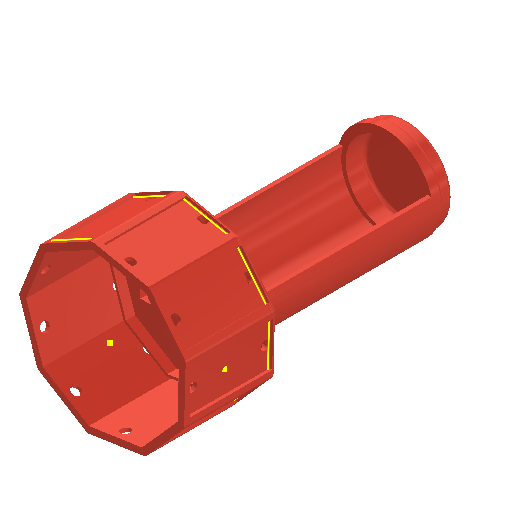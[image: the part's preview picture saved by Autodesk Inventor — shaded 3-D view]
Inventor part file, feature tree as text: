
AUTODESK INVENTOR PART (.ipt)
format: ipt  version: 2025 (Build 290162000, 162)  size: 719,872 bytes
history: native  units: in
note: dims shown in document units (in); Inventor stores cm internally (conversion verified against a paired STEP export)
features: sketch x28, extrude x24, fillet x7, direct_edit x2, pattern_circular x2, move_body x1, projected_geometry x1, other x1
ambient origin geometry x8: Origin, YZ Plane, XZ Plane, XY Plane, X Axis, Y Axis, Z Axis, Center Point
bodies: Solid1 (feature_tree), Body4 (feature_tree)
feature tree (66):
  direct_edit  "Direct Edit1"
  extrude  "Extrusion1"  Depth=0.2062in TaperAngle=0.0deg
  extrude  "Extrusion2"  Depth=0.1437in TaperAngle=0.0deg
  sketch  "Sketch3"  dims[d8=0.0787in d9=1.811in d10=0.0in]
  extrude  "Extrusion3"  Depth=0.0787in TaperAngle=0.0deg
  sketch  "Sketch6"  dims[d13=0.0591in d14=0.0in d15=0.1969in]
  extrude  "Extrusion4"  Depth=0.9449in
  extrude  "Extrusion5"  Depth=0.1969in
  pattern_circular  "Circular Pattern1"  Count=9  [1 undecoded]
  extrude  "Extrusion6"  Depth=0.0787in
  extrude  "Extrusion7"  Depth=0.0787in TaperAngle=0.0deg
  pattern_circular  "Circular Pattern2"  Count=9  [1 undecoded]
  fillet  "Fillet1"  Radius=0.1412in
  extrude  "Extrusion8"  Depth=0.063in
  extrude  "Extrusion9"  Depth=0.8312in TaperAngle=0.0deg
  extrude  "Extrusion10"  Depth=0.0787in
  extrude  "Extrusion11"  Depth=0.0787in TaperAngle=0.0deg
  direct_edit  "Direct Edit2"
  extrude  "Extrusion12"  Depth=1.1063in TaperAngle=0.0deg
  extrude  "Extrusion13"  Depth=0.4724in TaperAngle=0.0deg
  extrude  "Extrusion14"  Depth=0.0787in
  extrude  "Extrusion15"  Depth=1.2795in
  extrude  "Extrusion16"  Depth=0.0787in TaperAngle=0.0deg
  extrude  "Extrusion17"  Depth=0.0787in
  fillet  "Fillet2"  Radius=0.0787in
  fillet  "Fillet3"  Radius=0.0787in
  fillet  "Fillet4"  Radius=0.7338in
  fillet  "Fillet5"  Radius=0.3937in
  extrude  "Extrusion18"  Depth=0.0787in TaperAngle=0.0deg
  extrude  "Extrusion19"  Depth=0.1575in TaperAngle=0.0deg
  extrude  "Extrusion20"  Depth=0.1969in TaperAngle=0.0deg
  fillet  "Fillet6"  Radius=0.1781in
  sketch  "Sketch24"  dims[d78=1.3912in d79=0.1969in d80=0.0in d81=0.1781in d82=0.0in]
  extrude  "Extrusion22"  Depth=0.1575in
  fillet  "Fillet8"  Radius=1.9685in
  extrude  "Extrusion23"  Depth=1.9685in
  extrude  "Extrusion24"  [1 undecoded]
  extrude  "Extrusion25"  [1 undecoded]
  sketch  "Sketch30"
  sketch  "Sketch1"  dims[d0=0.0in d1=0.0in d2=-0.6875in d3=0.2062in d4=0.0in]
  sketch  "Sketch2"  dims[d5=1.1811in d6=0.1437in d7=0.0in]
  sketch  "Sketch5"  dims[d11=1.7323in d12=0.9449in]
  sketch  "Sketch7"  dims[d16=0.1969in]
  sketch  "Sketch8"  dims[d17=0.1841in d18=0.0in d19=3.5433in d20=2.4737in]
  sketch  "Sketch9"  dims[d22=0.0787in d23=0.315in]
  sketch  "Sketch10"  dims[d24=0.0787in d25=1.4409in d26=0.0in]
  sketch  "Sketch11"  dims[d27=1.9966in d28=0.0in d29=3.5433in d30=2.4737in d32=0.1412in]
  sketch  "Sketch12"  dims[d33=0.063in d34=0.063in]
  sketch  "Sketch13"  dims[d35=0.2756in d36=0.0in d37=0.8312in d38=0.0in]
  sketch  "Sketch14"  dims[d39=1.1063in d40=0.0in d41=0.0787in]
  sketch  "Sketch15"  dims[d42=0.0787in d43=0.1688in d44=0.0in]
  sketch  "Sketch16"  dims[d45=0.5187in d46=0.0in d47=1.1063in d48=0.0in]
  sketch  "Sketch17"  dims[d49=1.6535in d50=0.4724in d51=0.0in]
  sketch  "Sketch18"  dims[d52=0.0787in d53=0.0in d54=1.8898in]
  sketch  "Sketch19"  dims[d55=0.2963in d56=0.0in d57=1.2795in]
  sketch  "Sketch20"  dims[d58=1.3583in d59=0.0787in d60=0.0in]
  sketch  "Sketch21"  dims[d61=0.0787in d62=0.0787in d63=0.0787in d64=0.0787in d65=0.7338in d66=0.0in d67=0.3937in d68=0.0in]
  sketch  "Sketch22"  dims[d69=0.0787in d70=0.8312in d71=0.0in]
  sketch  "Sketch23"  dims[d72=0.0787in d76=0.1575in d77=0.0in]
  sketch  "Sketch26"  dims[d83=0.1575in d84=0.0in d85=0.0197in d86=1.9685in]
  sketch  "Sketch27"  dims[d87=0.0197in d88=1.9685in]
  sketch  "Sketch28"
  sketch  "Sketch29"
  move_body  "Move1"
  projected_geometry  "Project Cut Edges1"
  other  "Delete1"
note: 4 required parameter values undecoded (feature->parameter linkage not recoverable at this tier; creation-order binding heuristic only, values carry confidence <= 0.55)
